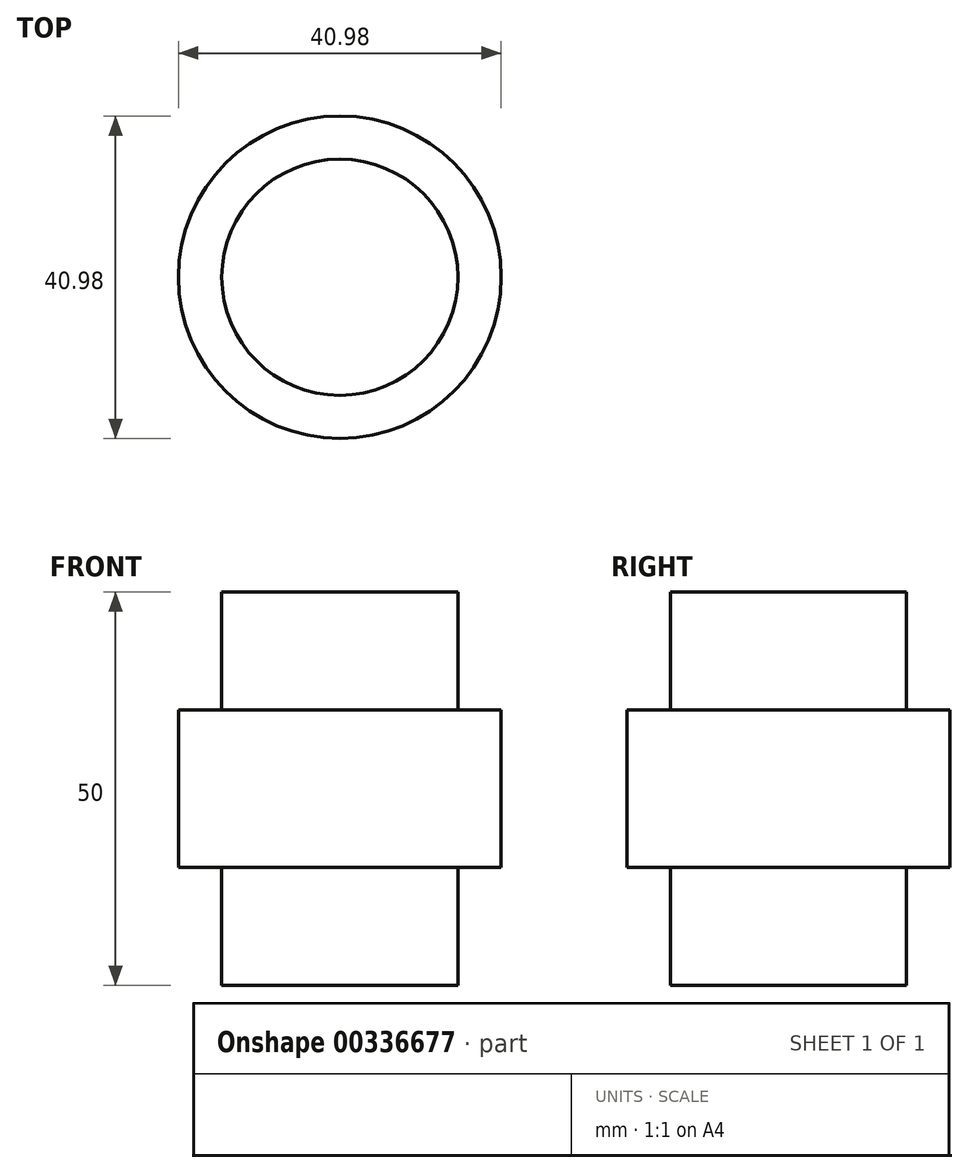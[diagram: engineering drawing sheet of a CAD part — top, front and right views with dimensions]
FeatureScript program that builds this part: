
annotation { "Feature Type Name" : "Feature", "Feature Type Description" : "" }
export const myFeature = defineFeature(function(context is Context, id is Id, definition is map)
    precondition{}
    {
        {
            var Q0;
            Q0=qCreatedBy(makeId("Top.planeOp"),FACE);
            var sketch = newSketch(context, id + "F0", { "sketchPlane" : qUnion([Q0])});
            skCircle(sketch, "E0", {"center": v(0, 0) * mm, "radius": 15 * mm});
            skSolve(sketch);
        }
        {
            var Q0;
            Q0 = qSketchRegion(id + "F0", true);
            extrude(context, id + "F1", {"entities" : qUnion([Q0]), "depth" : 15 * mm});
        }
        {
            var Q0;
            Q0=qCreatedBy(makeId("Top.planeOp"),FACE);
            var sketch = newSketch(context, id + "F2", { "sketchPlane" : qUnion([Q0])});
            skCircle(sketch, "E1", {"center": v(0, 0) * mm, "radius": 20.5 * mm});
            skSolve(sketch);
        }
        {
            var Q0;
            Q0 = qSketchRegion(id + "F2", true);
            extrude(context, id + "F3", {"entities" : qUnion([Q0]), "operationType" : NewBodyOperationType.ADD, "oppositeDirection" : true, "depth" : 20 * mm});
        }
        {
            var Q0;
            Q0=qCreatedBy(makeId("Top.planeOp"),FACE);
            var sketch = newSketch(context, id + "F4", { "sketchPlane" : qUnion([Q0])});
            skCircle(sketch, "E2", {"center": v(0, 0) * mm, "radius": 15 * mm});
            skSolve(sketch);
        }
        {
            var Q0;
            Q0 = qSketchRegion(id + "F4", true);
            extrude(context, id + "F5", {"entities" : qUnion([Q0]), "operationType" : NewBodyOperationType.ADD, "oppositeDirection" : true, "depth" : 35 * mm});
        }
    });
